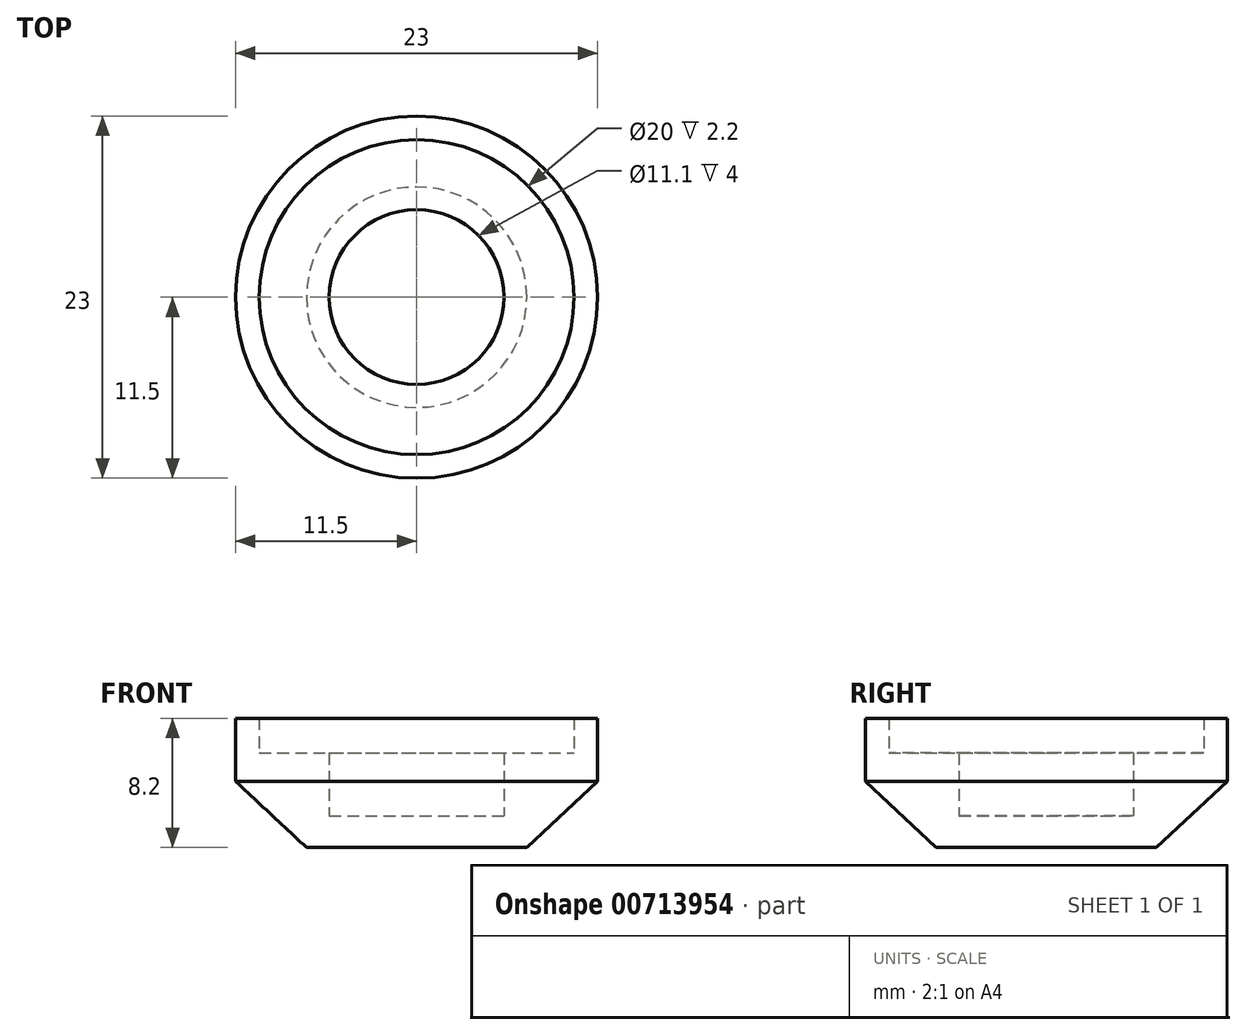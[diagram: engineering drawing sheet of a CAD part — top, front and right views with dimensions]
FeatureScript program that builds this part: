
annotation { "Feature Type Name" : "Feature", "Feature Type Description" : "" }
export const myFeature = defineFeature(function(context is Context, id is Id, definition is map)
    precondition{}
    {
        {
            var Q0;
            Q0=qCreatedBy(makeId("Front.planeOp"),FACE);
            var sketch = newSketch(context, id + "F0", { "sketchPlane" : qUnion([Q0])});
            skLineSegment(sketch, "E0", {"start": v(-10, 8.2) * mm, "end": v(-11.5, 8.2) * mm});
            skLineSegment(sketch, "E1", {"start": v(-11.5, 8.2) * mm, "end": v(-11.5, 4.2) * mm});
            skLineSegment(sketch, "E2", {"start": v(-11.5, 4.2) * mm, "end": v(-7, 0) * mm});
            skLineSegment(sketch, "E3", {"start": v(-7, 0) * mm, "end": v(0, 0) * mm});
            skLineSegment(sketch, "E4", {"start": v(0, 0) * mm, "end": v(0, 2) * mm});
            skLineSegment(sketch, "E5", {"start": v(0, 2) * mm, "end": v(-5.55, 2) * mm});
            skLineSegment(sketch, "E6", {"start": v(-5.55, 2) * mm, "end": v(-5.55, 6) * mm});
            skLineSegment(sketch, "E7", {"start": v(-5.55, 6) * mm, "end": v(-10, 6) * mm});
            skLineSegment(sketch, "E8", {"start": v(-10, 6) * mm, "end": v(-10, 8.2) * mm});
            skSolve(sketch);
        }
        {
            var Q0;
            Q0=makeQuery(id+"F0.imprint","IMPRINT",FACE,{"disambiguationData":[TD([[makeQuery(id+"F0.imprint","IMPRINT",EDGE,{"derivedFrom":sQuery(id+"F0.wireOp",EDGE,"E0")}),1.0]])]});
            var Q1;
            Q1=sQuery(id+"F0.wireOp",EDGE,"E4");
            revolve(context, id + "F1", {"surfaceOperationType" : NewSurfaceOperationType.NEW, "entities" : qUnion([Q0]), "axis" : qUnion([Q1]), "revolveType" : RevolveType.FULL});
        }
    });
